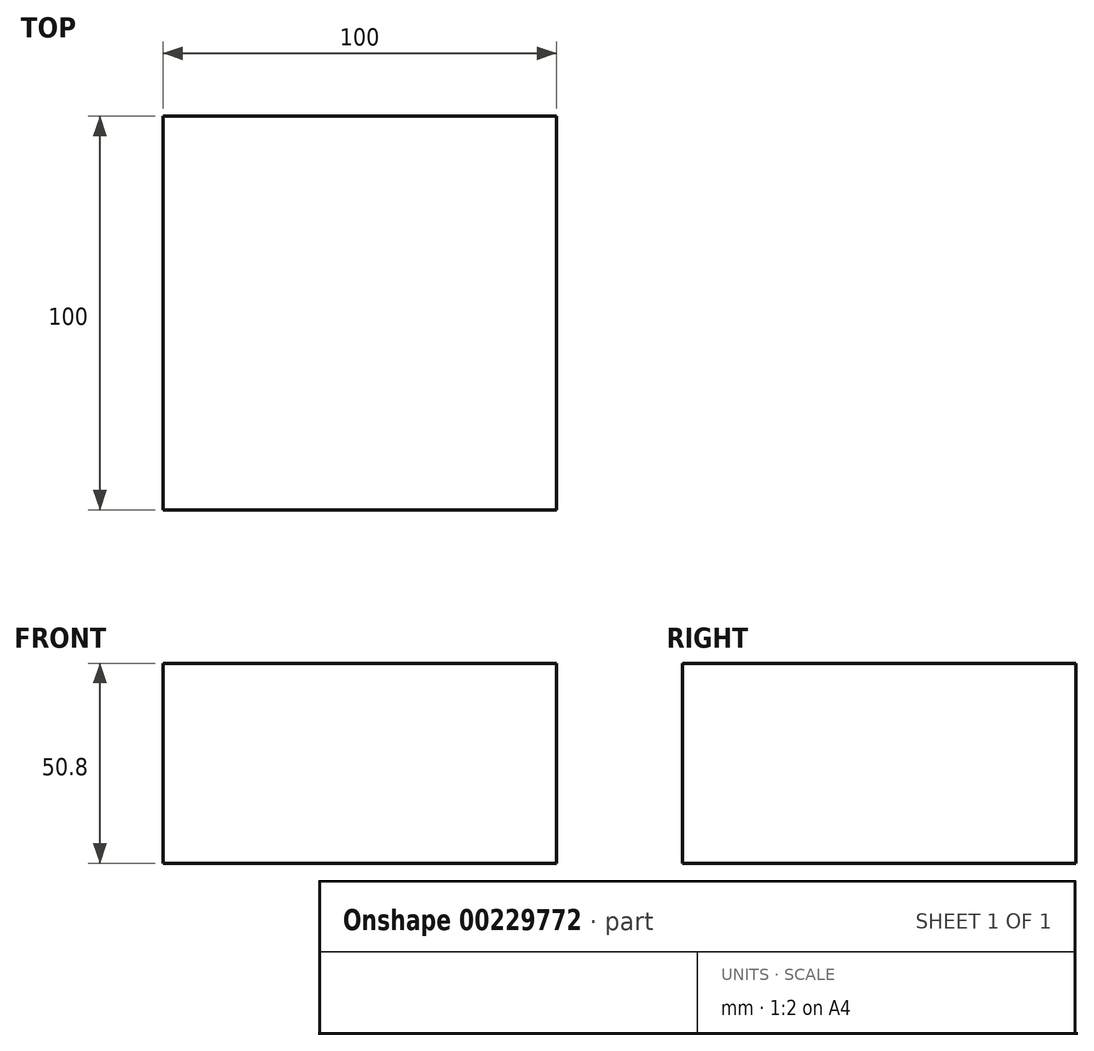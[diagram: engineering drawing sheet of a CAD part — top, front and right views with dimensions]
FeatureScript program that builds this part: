
annotation { "Feature Type Name" : "Feature", "Feature Type Description" : "" }
export const myFeature = defineFeature(function(context is Context, id is Id, definition is map)
    precondition{}
    {
        {
            var Q0;
            Q0=qCreatedBy(makeId("Top.planeOp"),FACE);
            var sketch = newSketch(context, id + "F0", { "sketchPlane" : qUnion([Q0])});
            skLineSegment(sketch, "E0.bottom", {"start": v(50, -50) * mm, "end": v(-50, -50) * mm});
            skLineSegment(sketch, "E0.top", {"start": v(50, 50) * mm, "end": v(-50, 50) * mm});
            skLineSegment(sketch, "E0.left", {"start": v(50, -50) * mm, "end": v(50, 50) * mm});
            skLineSegment(sketch, "E0.right", {"start": v(-50, -50) * mm, "end": v(-50, 50) * mm});
            skPoint(sketch, "E0.middle", {"position": v(0, 0) * mm});
            skSolve(sketch);
        }
        {
            var Q0;
            Q0 = qSketchRegion(id + "F0", true);
            extrude(context, id + "F1", {"entities" : qUnion([Q0]), "depth" : 50.8 * mm, "offsetDistance" : 25.4 * mm});
        }
    });
